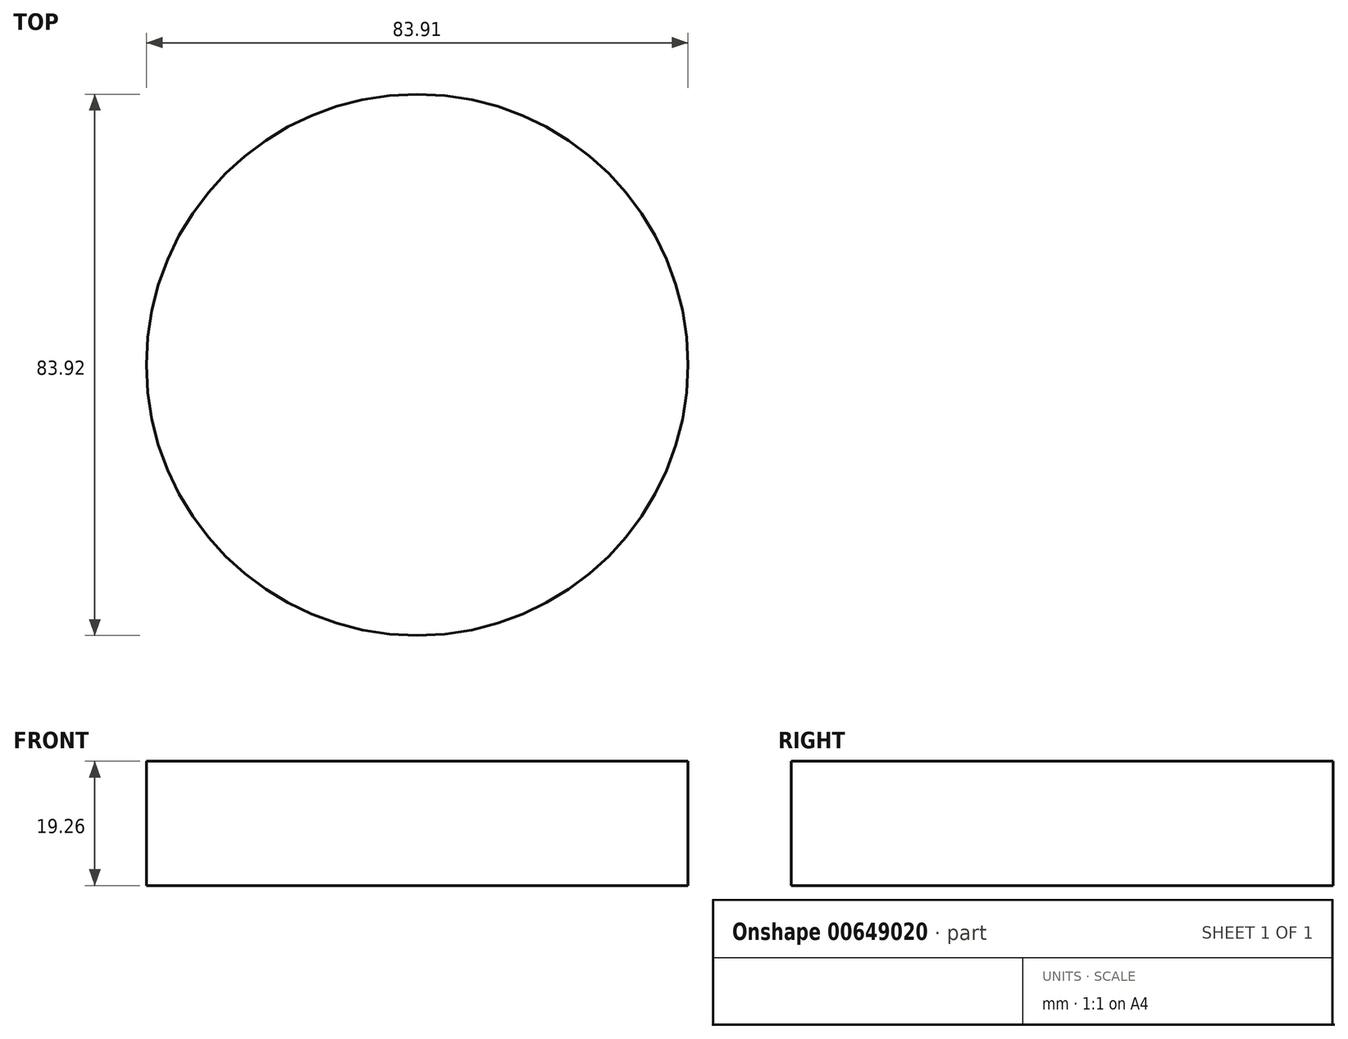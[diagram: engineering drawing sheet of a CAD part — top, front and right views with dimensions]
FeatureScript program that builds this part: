
annotation { "Feature Type Name" : "Feature", "Feature Type Description" : "" }
export const myFeature = defineFeature(function(context is Context, id is Id, definition is map)
    precondition{}
    {
        {
            var Q0;
            Q0=qCreatedBy(makeId("Top.planeOp"),FACE);
            var sketch = newSketch(context, id + "F0", { "sketchPlane" : qUnion([Q0])});
            skCircle(sketch, "E0", {"center": v(-16.42, 28.85) * mm, "radius": 41.96 * mm});
            skSolve(sketch);
        }
        {
            var Q0;
            Q0=makeQuery(id+"F0.imprint","IMPRINT",FACE,{"disambiguationData":[TD([[makeQuery(id+"F0.imprint","IMPRINT",EDGE,{"derivedFrom":sQuery(id+"F0.wireOp",EDGE,"E0")}),1.0]])]});
            extrude(context, id + "F1", {"entities" : qUnion([Q0]), "depth" : 19.26 * mm, "offsetDistance" : 25.4 * mm});
        }
    });
